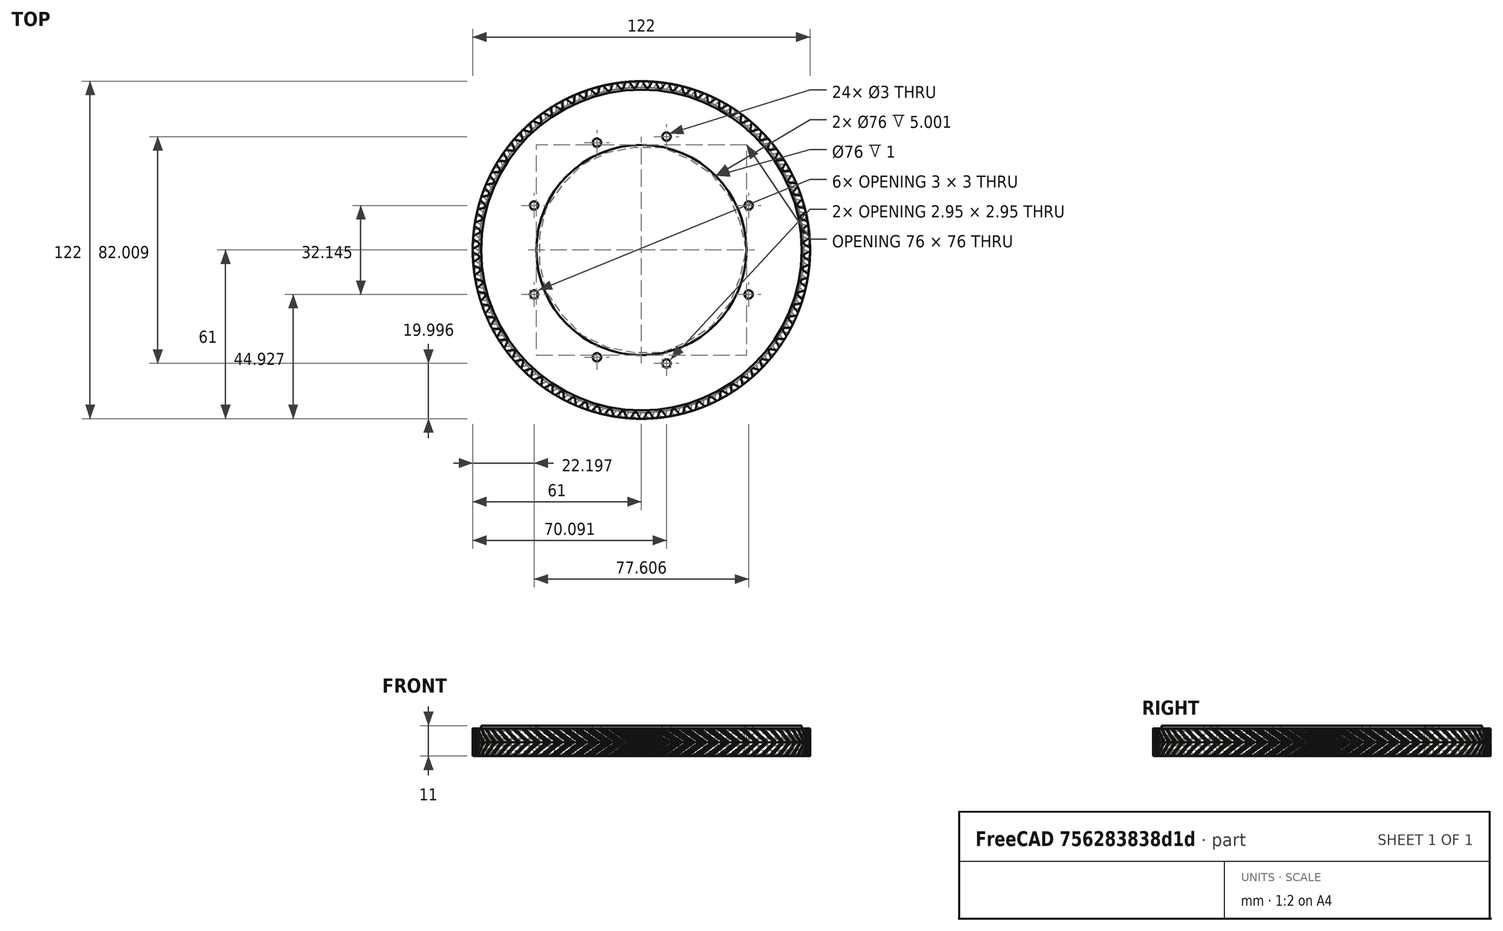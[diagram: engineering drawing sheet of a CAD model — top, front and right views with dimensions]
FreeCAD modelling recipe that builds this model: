
FCSTD DOCUMENT  (FreeCAD 0.19R24276 (Git))
Label: bazovina-part-D_ozubo_008
License: All rights reserved
LicenseURL: http://en.wikipedia.org/wiki/All_rights_reserved
objects: Part::Cylinder×26, Part::Cut×5, Part::Compound×5, Part::FeaturePython×3, Mesh::Feature×1
note: 39 computed .brp shape members not serialized (recipe doc carries the construction recipe); baked Part::Feature solids carry a one-line shape summary decoded from their .brp

FEATURE [Part::FeaturePython] wormgear022  # WARN: FeaturePython — macro-defined, semantics opaque (R4)
  AttacherType = Attacher::AttachEngine3D
  Placement = pos=(0,0,100) rot=(0,0,1;0rad)
  beta = 33.6901
  clearance = 0.25
  diameter = 120
  head = 0
  height = 5
  module = 1
  pressure_angle = 20
  reverse_pitch = true
  teeth = 80
  version = 0.0.3
FEATURE [Part::FeaturePython] wormgear023  # WARN: FeaturePython — macro-defined, semantics opaque (R4)
  AttacherType = Attacher::AttachEngine3D
  Placement = pos=(0,0,95) rot=(0,0,1;0.032289rad)
  beta = 33.6901
  clearance = 0.25
  diameter = 120
  head = 0
  height = 5
  module = 1
  pressure_angle = 20
  reverse_pitch = false
  teeth = 80
  version = 0.0.3
FEATURE [Part::Cylinder] Cylinder289  label="Válec289"
  Angle = 360
  AttacherType = Attacher::AttachEngine3D
  Height = 20
  Placement = pos=(0,0,91) rot=(0,0,1;0rad)
  Radius = 38
FEATURE [Part::Cut] Cut128
  Base = -> wormgear022
  Placement = pos=(0,0,-63) rot=(0,0,1;0rad)
  Tool = -> Cylinder289
FEATURE [Part::Cylinder] Cylinder290  label="Válec290"
  Angle = 360
  AttacherType = Attacher::AttachEngine3D
  Height = 20
  Placement = pos=(0,0,91) rot=(0,0,1;0rad)
  Radius = 38
FEATURE [Part::Cut] Cut127
  Base = -> wormgear023
  Placement = pos=(0,0,-63) rot=(0,0,1;0rad)
  Tool = -> Cylinder290
FEATURE [Part::Cylinder] Cylinder461  label="Válec461"
  Angle = 360
  AttacherType = Attacher::AttachEngine3D
  Height = 100
  Placement = pos=(38.8029,-16.0727,0) rot=(0,0,1;1.5708rad)
  Radius = 1.5
FEATURE [Part::Cylinder] Cylinder454  label="Válec454"
  Angle = 360
  AttacherType = Attacher::AttachEngine3D
  Height = 100
  Placement = pos=(38.8029,16.0727,0) rot=(0,0,1;2.35619rad)
  Radius = 1.5
FEATURE [Part::Cylinder] Cylinder455  label="Válec455"
  Angle = 360
  AttacherType = Attacher::AttachEngine3D
  Height = 100
  Placement = pos=(9.09046,41.0044,0) rot=(0,0,1;3.31613rad)
  Radius = 1.5
FEATURE [Part::Cylinder] Cylinder456  label="Válec456"
  Angle = 360
  AttacherType = Attacher::AttachEngine3D
  Height = 100
  Placement = pos=(-16.0727,38.8029,0) rot=(0,0,1;3.92699rad)
  Radius = 1.5
FEATURE [Part::Cylinder] Cylinder457  label="Válec457"
  Angle = 360
  AttacherType = Attacher::AttachEngine3D
  Height = 100
  Placement = pos=(-38.8029,16.0727,0) rot=(0,0,-1;1.5708rad)
  Radius = 1.5
FEATURE [Part::Cylinder] Cylinder452  label="Válec452"
  Angle = 360
  AttacherType = Attacher::AttachEngine3D
  Height = 100
  Placement = pos=(9.09046,-41.0044,0) rot=(0,0,1;0.610865rad)
  Radius = 1.5
FEATURE [Part::Cylinder] Cylinder453  label="Válec453"
  Angle = 360
  AttacherType = Attacher::AttachEngine3D
  Height = 100
  Placement = pos=(38.8029,-16.0727,0) rot=(0,0,1;1.5708rad)
  Radius = 1.5
FEATURE [Part::Cylinder] Cylinder459  label="Válec459"
  Angle = 360
  AttacherType = Attacher::AttachEngine3D
  Height = 100
  Placement = pos=(-16.0727,-38.8029,0) rot=(0,0,1;0rad)
  Radius = 1.5
FEATURE [Part::Cylinder] Cylinder458  label="Válec458"
  Angle = 360
  AttacherType = Attacher::AttachEngine3D
  Height = 100
  Placement = pos=(-38.8029,-16.0727,0) rot=(0,0,-1;0.785398rad)
  Radius = 1.5
FEATURE [Part::Compound] Compound326
  Links = -> [Cylinder452,Cylinder453,Cylinder454,Cylinder455,Cylinder456,Cylinder457,Cylinder458,Cylinder459]
FEATURE [Part::Cut] Cut171
  Base = -> Cut128
  Tool = -> Compound326
FEATURE [Part::Cylinder] Cylinder460  label="Válec460"
  Angle = 360
  AttacherType = Attacher::AttachEngine3D
  Height = 100
  Placement = pos=(9.09046,-41.0044,0) rot=(0,0,1;0.610865rad)
  Radius = 1.5
FEATURE [Part::Cylinder] Cylinder463  label="Válec463"
  Angle = 360
  AttacherType = Attacher::AttachEngine3D
  Height = 100
  Placement = pos=(9.09046,41.0044,0) rot=(0,0,1;3.31613rad)
  Radius = 1.5
FEATURE [Part::Cylinder] Cylinder464  label="Válec464"
  Angle = 360
  AttacherType = Attacher::AttachEngine3D
  Height = 100
  Placement = pos=(-16.0727,38.8029,0) rot=(0,0,1;3.92699rad)
  Radius = 1.5
FEATURE [Part::Cylinder] Cylinder465  label="Válec465"
  Angle = 360
  AttacherType = Attacher::AttachEngine3D
  Height = 100
  Placement = pos=(-38.8029,16.0727,0) rot=(0,0,-1;1.5708rad)
  Radius = 1.5
FEATURE [Part::Cylinder] Cylinder466  label="Válec466"
  Angle = 360
  AttacherType = Attacher::AttachEngine3D
  Height = 100
  Placement = pos=(-38.8029,-16.0727,0) rot=(0,0,-1;0.785398rad)
  Radius = 1.5
FEATURE [Part::Cylinder] Cylinder462  label="Válec462"
  Angle = 360
  AttacherType = Attacher::AttachEngine3D
  Height = 100
  Placement = pos=(38.8029,16.0727,0) rot=(0,0,1;2.35619rad)
  Radius = 1.5
FEATURE [Part::Cylinder] Cylinder467  label="Válec467"
  Angle = 360
  AttacherType = Attacher::AttachEngine3D
  Height = 100
  Placement = pos=(-16.0727,-38.8029,0) rot=(0,0,1;0rad)
  Radius = 1.5
FEATURE [Part::Compound] Compound327
  Links = -> [Cylinder460,Cylinder461,Cylinder462,Cylinder463,Cylinder464,Cylinder465,Cylinder466,Cylinder467]
FEATURE [Part::Cut] Cut172
  Base = -> Cut127
  Tool = -> Compound327
FEATURE [Part::Compound] Compound335  label="bazovina-part-D_ozubo2"
  Links = -> [Cut171,Cut172]
FEATURE [Part::Cylinder] Cylinder756  label="Válec756"
  Angle = 360
  AttacherType = Attacher::AttachEngine3D
  Height = 100
  Placement = pos=(-16.0727,-38.8029,0) rot=(0,0,1;0rad)
  Radius = 1.5
FEATURE [Part::Cylinder] Cylinder757  label="Válec757"
  Angle = 360
  AttacherType = Attacher::AttachEngine3D
  Height = 100
  Placement = pos=(41.0044,-9.09046,0) rot=(0,0,1;1.74533rad)
  Radius = 1.5
FEATURE [Part::Cylinder] Cylinder754  label="Válec754"
  Angle = 360
  AttacherType = Attacher::AttachEngine3D
  Height = 100
  Placement = pos=(-38.8029,16.0727,0) rot=(0,0,-1;1.5708rad)
  Radius = 1.5
FEATURE [Part::Cylinder] Cylinder755  label="Válec755"
  Angle = 360
  AttacherType = Attacher::AttachEngine3D
  Height = 100
  Placement = pos=(38.8029,16.0727,0) rot=(0,0,1;2.35619rad)
  Radius = 1.5
FEATURE [Part::FeaturePython] Tube079  # WARN: FeaturePython — macro-defined, semantics opaque (R4)
  AttacherType = Attacher::AttachEngine3D
  Height = 1
  InnerRadius = 38
  OuterRadius = 58
  Placement = pos=(0,0,42) rot=(0,0,1;0rad)
FEATURE [Part::Cylinder] Cylinder758  label="Válec758"
  Angle = 360
  AttacherType = Attacher::AttachEngine3D
  Height = 100
  Placement = pos=(-41.0044,-9.09046,0) rot=(0,0,-1;0.959931rad)
  Radius = 1.5
FEATURE [Part::Cylinder] Cylinder761  label="Válec761"
  Angle = 360
  AttacherType = Attacher::AttachEngine3D
  Height = 100
  Placement = pos=(-16.0727,38.8029,0) rot=(0,0,1;3.92699rad)
  Radius = 1.5
FEATURE [Part::Cylinder] Cylinder759  label="Válec759"
  Angle = 360
  AttacherType = Attacher::AttachEngine3D
  Height = 100
  Placement = pos=(16.0727,38.8029,0) rot=(0,0,1;3.14159rad)
  Radius = 1.5
FEATURE [Part::Cylinder] Cylinder760  label="Válec760"
  Angle = 360
  AttacherType = Attacher::AttachEngine3D
  Height = 100
  Placement = pos=(16.0727,-38.8029,0) rot=(0,0,1;0.785398rad)
  Radius = 1.5
FEATURE [Part::Compound] Compound709
  Links = -> [Cylinder760,Cylinder757,Cylinder755,Cylinder759,Cylinder761,Cylinder754,Cylinder758,Cylinder756]
FEATURE [Part::Cut] Cut325  label="bazovina_part-F_washer001"
  Base = -> Tube079
  Placement = pos=(0,0,0) rot=(0,0,1;1.5708rad)
  Tool = -> Compound709
FEATURE [Part::Compound] Compound  label="bazovina_part-D_ozubo-washer"
  Links = -> [Compound335,Cut325]
FEATURE [Mesh::Feature] Mesh  label="bazovina_part-D_ozubo-washer (Meshed)"
